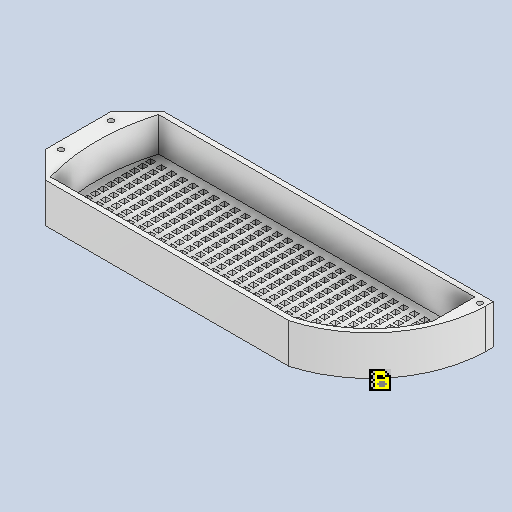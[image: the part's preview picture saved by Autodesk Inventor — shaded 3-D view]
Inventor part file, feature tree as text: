
AUTODESK INVENTOR PART (.ipt)
format: ipt  version: 2024 (Build 280153000, 153)  size: 2,126,336 bytes
history: native  units: mm
features: sketch x9, extrude x7
ambient origin geometry x8: Origin, YZ Plane, XZ Plane, XY Plane, X Axis, Y Axis, Z Axis, Center Point
bodies: Body1 (feature_tree)
feature tree (16):
  extrude  "Extrusion2"  TaperAngle=45.0deg  [1 undecoded]
  sketch  "Sketch3"  dims[d9=15.0mm d10=0.0mm d11=2.0mm]
  sketch  "Sketch4"  dims[d12=2.0mm d23=15.0mm d24=0.0mm]
  extrude  "Extrusion3"  Depth=2.0mm
  extrude  "Extrusion4"  Depth=15.0mm TaperAngle=0.0deg
  sketch  "Sketch11"  dims[d25=13.0mm d26=0.0mm d34=2.0mm]
  extrude  "Extrusion8"  Depth=2.0mm
  sketch  "Sketch13"  dims[d64=1.5mm d81=3.0mm]
  extrude  "Extrusion9"  Depth=2.0mm
  extrude  "Extrusion12"  Depth=3.0mm
  extrude  "Extrusion13"  Depth=2.0mm
  sketch  "Sketch2"  dims[d3=45.0deg d4=45.0deg]
  sketch  "Sketch12"  dims[d62=2.0mm d63=2.0mm]
  sketch  "Sketch15"  dims[d82=3.0mm d83=2.0mm]
  sketch  "Sketch20"  dims[d84=2.0mm]
  sketch  "Sketch21"  dims[d85=240.0mm d87=4.0mm d88=120.0mm d90=3.0mm d93=10.0mm d94=0.0mm d98=2.0mm d99=2.0mm d100=2.0mm d101=0.0mm d102=30.0mm d104=4.0mm d105=100.0mm d107=3.0mm d110=2.0mm d112=4.0mm d113=0.0mm d115=2.0mm d116=1.0mm d118=2.0mm d119=2.0mm d122=2.0mm d123=2.0mm d124=2.0mm d125=2.0mm d126=2.0mm d127=2.0mm d128=2.0mm d129=2.0mm d130=1.0mm d131=10.0mm d132=0.0mm d138=2.0mm d139=13.0mm d140=0.0mm d141=2.0mm d142=3.0mm d143=3.0mm d144=2.0mm d145=3.0mm d146=13.0mm d147=2.0mm d148=3.0mm d149=13.0mm d150=3.0mm d151=0.0mm d152=2.0mm d153=120.0mm d155=3.0mm d156=60.0mm d158=4.0mm]
note: 1 required parameter value undecoded (feature->parameter linkage not recoverable at this tier; creation-order binding heuristic only, values carry confidence <= 0.55)
